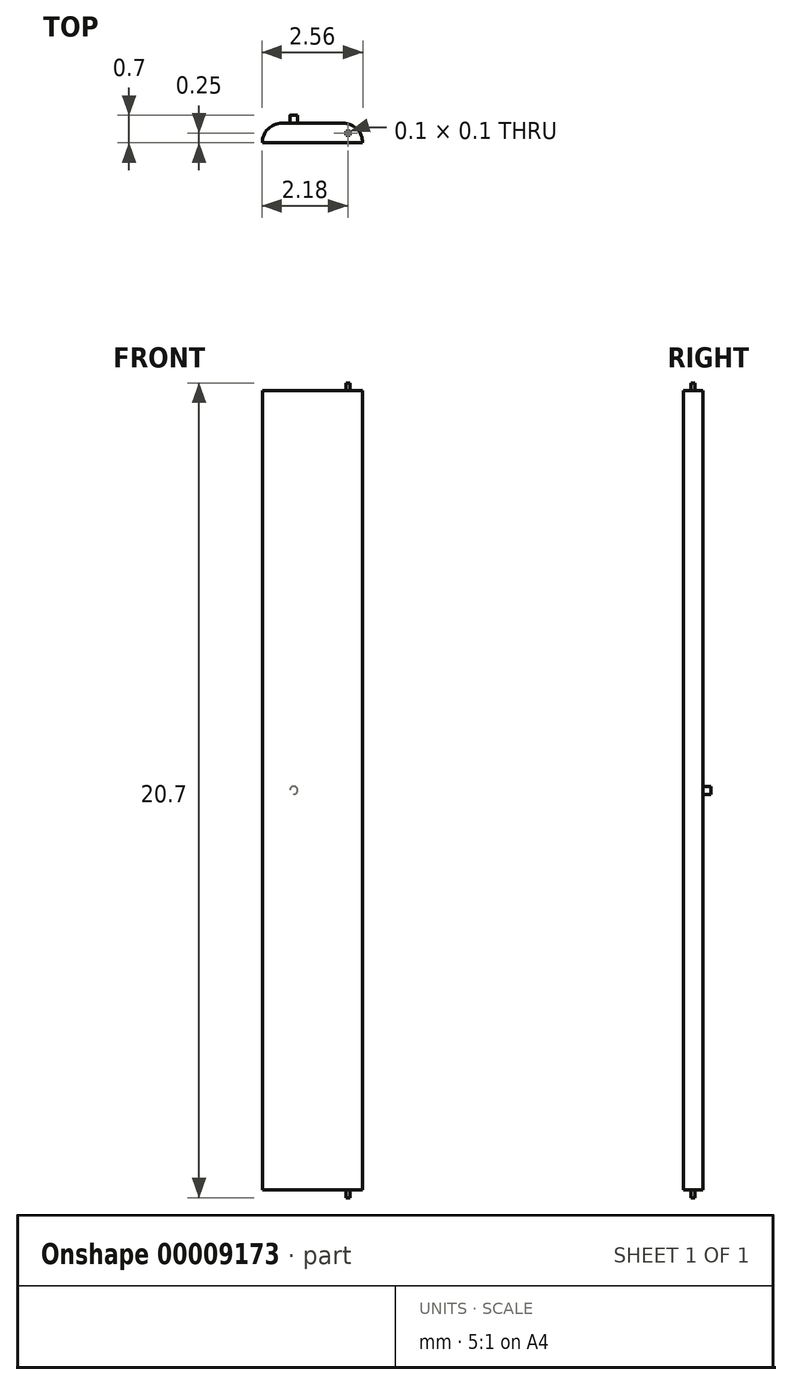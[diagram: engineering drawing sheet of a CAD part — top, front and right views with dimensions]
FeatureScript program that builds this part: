
annotation { "Feature Type Name" : "Feature", "Feature Type Description" : "" }
export const myFeature = defineFeature(function(context is Context, id is Id, definition is map)
    precondition{}
    {
        {
            var Q0;
            Q0=qCreatedBy(makeId("Top.planeOp"),FACE);
            var sketch = newSketch(context, id + "F0", { "sketchPlane" : qUnion([Q0])});
            skLineSegment(sketch, "E0.rect.bottom", {"start": v(1.28, 0.25) * mm, "end": v(-1.27, 0.25) * mm});
            skLineSegment(sketch, "E0.rect.top", {"start": v(1.27, -0.25) * mm, "end": v(-1.27, -0.25) * mm});
            skLineSegment(sketch, "E0.rect.left", {"start": v(1.27, 0.25) * mm, "end": v(1.27, -0.25) * mm});
            skLineSegment(sketch, "E0.rect.right", {"start": v(-1.27, 0.25) * mm, "end": v(-1.27, -0.25) * mm});
            skPoint(sketch, "E0.rect.middle", {"position": v(0, 0) * mm});
            skSolve(sketch);
        }
        {
            var Q0;
            Q0=makeQuery(id+"F0.imprint","IMPRINT",FACE,{"disambiguationData":[TD([[makeQuery(id+"F0.imprint","IMPRINT",EDGE,{"derivedFrom":sQuery(id+"F0.wireOp",EDGE,"E0.rect.bottom")}),1.0]])]});
            extrude(context, id + "F1", {"entities" : qUnion([Q0]), "depth" : 20.3 * mm});
        }
        {
            var Q0;
            Q0=makeQuery(id+"F1.opExtrude","SWEPT_EDGE",EDGE,{"disambiguationData":[OSD([sQuery(id+"F0.wireOp",EDGE,"E0.rect.bottom"),sQuery(id+"F0.wireOp",EDGE,"E0.rect.left")])]});
            var Q1;
            Q1=makeQuery(id+"F1.opExtrude","SWEPT_EDGE",EDGE,{"disambiguationData":[OSD([sQuery(id+"F0.wireOp",EDGE,"E0.rect.bottom"),sQuery(id+"F0.wireOp",EDGE,"E0.rect.right")])]});
            fillet(context, id + "F2", {"entities" : qUnion([Q0, Q1]), "radius" : 0.5 * mm, "tangentPropagation" : true, "allowEdgeOverflow" : false});
        }
        {
            var Q0;
            Q0=makeQuery(id+"F1.opExtrude","SWEPT_FACE",FACE,{"disambiguationData":[OSD([sQuery(id+"F0.wireOp",EDGE,"E0.rect.bottom")])]});
            var sketch = newSketch(context, id + "F3", { "sketchPlane" : qUnion([Q0])});
            skCircle(sketch, "E1", {"center": v(0.48, 10.15) * mm, "radius": 0.1 * mm});
            skSolve(sketch);
        }
        {
            var Q0;
            Q0 = qSketchRegion(id + "F3", true);
            extrude(context, id + "F4", {"entities" : qUnion([Q0]), "operationType" : NewBodyOperationType.ADD, "depth" : 0.2 * mm});
        }
        {
            var Q0;
            Q0=makeQuery(id+"F1.opExtrude","CAP_FACE",FACE,{"disambiguationData":[OSD([sQuery(id+"F0.wireOp",EDGE,"E0.rect.bottom"),sQuery(id+"F0.wireOp",EDGE,"E0.rect.top"),sQuery(id+"F0.wireOp",EDGE,"E0.rect.left"),sQuery(id+"F0.wireOp",EDGE,"E0.rect.right")])],"isStart":true});
            var sketch = newSketch(context, id + "F5", { "sketchPlane" : qUnion([Q0])});
            skLineSegment(sketch, "E2.rect.bottom", {"start": v(0.95, 0.05) * mm, "end": v(0.85, 0.05) * mm});
            skLineSegment(sketch, "E2.rect.top", {"start": v(0.95, -0.05) * mm, "end": v(0.85, -0.05) * mm});
            skLineSegment(sketch, "E2.rect.left", {"start": v(0.95, 0.05) * mm, "end": v(0.95, -0.05) * mm});
            skLineSegment(sketch, "E2.rect.right", {"start": v(0.85, 0.05) * mm, "end": v(0.85, -0.05) * mm});
            skPoint(sketch, "E2.rect.middle", {"position": v(0.9, 0) * mm});
            skSolve(sketch);
        }
        {
            var Q0;
            Q0=makeQuery(id+"F5.imprint","IMPRINT",FACE,{"disambiguationData":[TD([[makeQuery(id+"F5.imprint","IMPRINT",EDGE,{"derivedFrom":sQuery(id+"F5.wireOp",EDGE,"E2.rect.bottom")}),1.0]])]});
            extrude(context, id + "F6", {"entities" : qUnion([Q0]), "operationType" : NewBodyOperationType.ADD, "depth" : 0.2 * mm});
        }
        {
            var Q0;
            Q0=makeQuery(id+"F1.opExtrude","CAP_FACE",FACE,{"disambiguationData":[OSD([sQuery(id+"F0.wireOp",EDGE,"E0.rect.bottom"),sQuery(id+"F0.wireOp",EDGE,"E0.rect.top"),sQuery(id+"F0.wireOp",EDGE,"E0.rect.left"),sQuery(id+"F0.wireOp",EDGE,"E0.rect.right")])],"isStart":false});
            var sketch = newSketch(context, id + "F7", { "sketchPlane" : qUnion([Q0])});
            skLineSegment(sketch, "E3.rect.bottom", {"start": v(0.95, 0.05) * mm, "end": v(0.85, 0.05) * mm});
            skLineSegment(sketch, "E3.rect.top", {"start": v(0.95, -0.05) * mm, "end": v(0.85, -0.05) * mm});
            skLineSegment(sketch, "E3.rect.left", {"start": v(0.95, 0.05) * mm, "end": v(0.95, -0.05) * mm});
            skLineSegment(sketch, "E3.rect.right", {"start": v(0.85, 0.05) * mm, "end": v(0.85, -0.05) * mm});
            skPoint(sketch, "E3.rect.middle", {"position": v(0.9, 0) * mm});
            skSolve(sketch);
        }
        {
            var Q0;
            Q0=makeQuery(id+"F7.imprint","IMPRINT",FACE,{"disambiguationData":[TD([[makeQuery(id+"F7.imprint","IMPRINT",EDGE,{"derivedFrom":sQuery(id+"F7.wireOp",EDGE,"E3.rect.bottom")}),1.0]])]});
            extrude(context, id + "F8", {"entities" : qUnion([Q0]), "operationType" : NewBodyOperationType.ADD, "depth" : 0.2 * mm});
        }
    });
